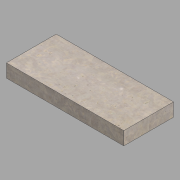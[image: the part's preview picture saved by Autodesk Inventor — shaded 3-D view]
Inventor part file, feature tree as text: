
AUTODESK INVENTOR PART (.ipt)
format: ipt  version: 2022.2 (Build 262287000, 287)  size: 109,568 bytes
history: native  units: in
note: dims shown in document units (in); Inventor stores cm internally (conversion verified against a paired STEP export)
features: extrude x1, sketch x1
ambient origin geometry x8: Origin, YZ Plane, XZ Plane, XY Plane, X Axis, Y Axis, Z Axis, Center Point
bodies: Solid1 (feature_tree)
feature tree (2):
  extrude  "Extrusion1"  Depth=15.0in
  sketch  "Sketch1"  dims[d0=4.0in d1=15.0in d2=35.375in d3=0.0in]
